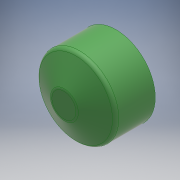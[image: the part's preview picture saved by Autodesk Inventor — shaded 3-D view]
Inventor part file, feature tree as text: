
AUTODESK INVENTOR PART (.ipt)
format: ipt  version: 2019 (Build 230136000, 136)  size: 150,528 bytes
history: native  units: mm
features: other x1, revolve x1, fillet x1, sketch x1
ambient origin geometry x8: Origin, YZ Plane, XZ Plane, XY Plane, X Axis, Y Axis, Z Axis, Center Point
bodies: Body1 (feature_tree)
feature tree (4):
  other  "Твердое тело1"
  revolve  "Вращение1"
  fillet  "Сопряжение1"  Radius=18.0mm
  sketch  "Эскиз1"
